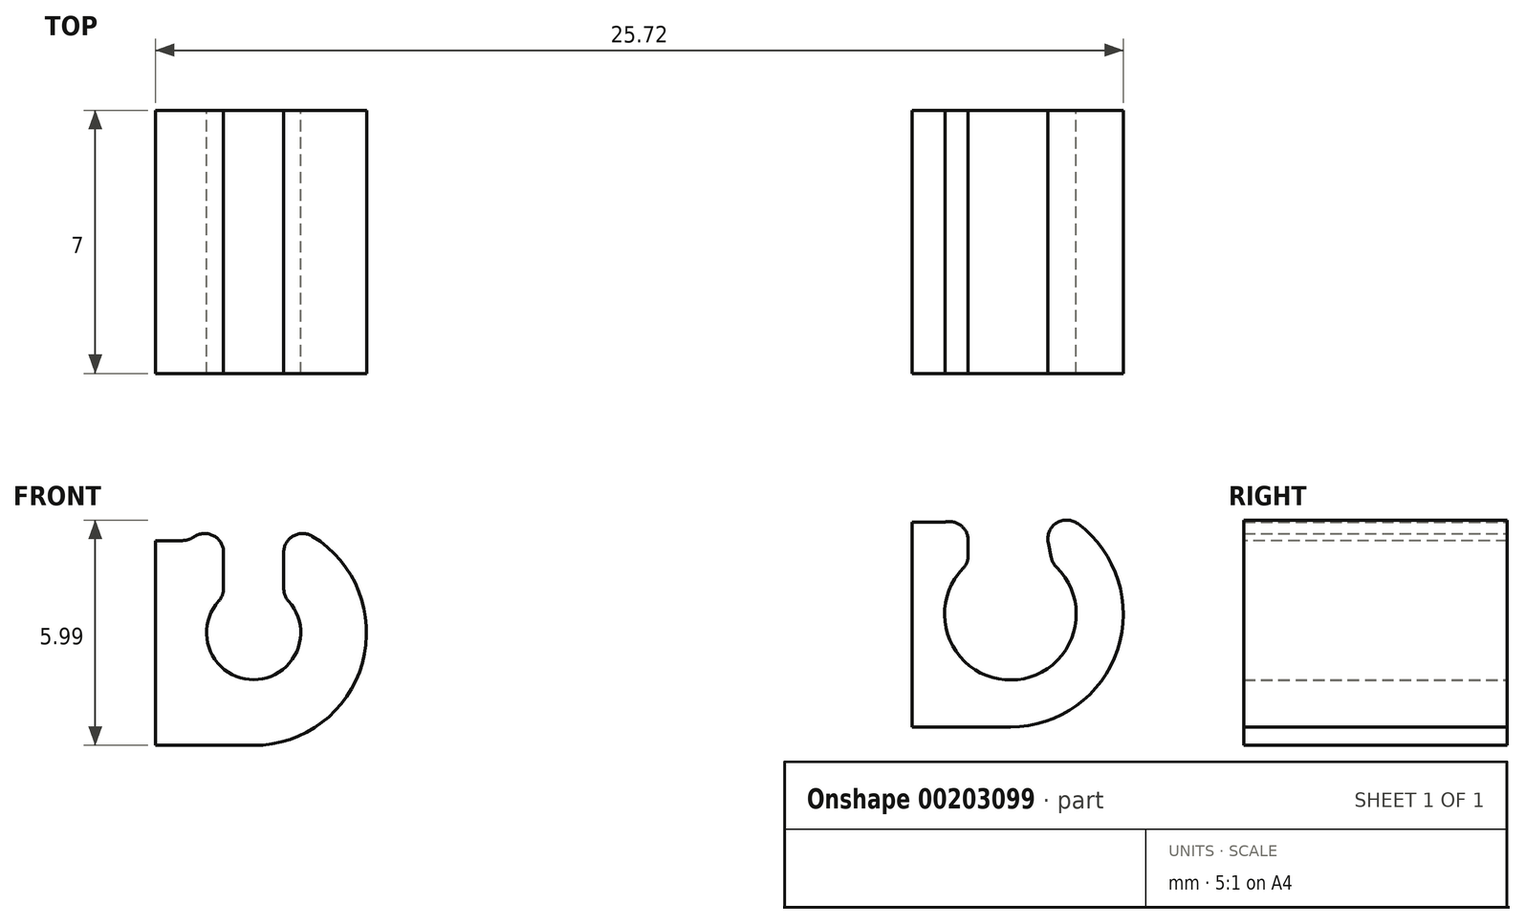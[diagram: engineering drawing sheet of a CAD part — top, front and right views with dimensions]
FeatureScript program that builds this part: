
annotation { "Feature Type Name" : "Feature", "Feature Type Description" : "" }
export const myFeature = defineFeature(function(context is Context, id is Id, definition is map)
    precondition{}
    {
        {
            var Q0;
            Q0=qCreatedBy(makeId("Front.planeOp"),FACE);
            var sketch = newSketch(context, id + "F0", { "sketchPlane" : qUnion([Q0])});
            skArc(sketch, "E0", {"start": v(-0.8, 2.9) * mm, "mid": v(-1.29, 2.71) * mm, "end": v(-1.73, 2.45) * mm});
            skArc(sketch, "E1", {"start": v(-0.8, 0.96) * mm, "mid": v(0, -1.25) * mm, "end": v(0.8, 0.96) * mm});
            skLineSegment(sketch, "E2", {"start": v(-0.8, 2.9) * mm, "end": v(-0.8, 0.96) * mm});
            skLineSegment(sketch, "E3.MirrorCS", {"start": v(0.8, 2.9) * mm, "end": v(0.8, 0.96) * mm});
            skLineSegment(sketch, "E4", {"start": v(-2.6, 1.48) * mm, "end": v(-2.6, -1.48) * mm});
            skArc(sketch, "E5.trimOffspring", {"start": v(0, -3) * mm, "mid": v(2.97, -0.4) * mm, "end": v(0.8, 2.9) * mm});
            skLineSegment(sketch, "E6", {"start": v(-2.6, 1.48) * mm, "end": v(-2.6, 2.45) * mm});
            skLineSegment(sketch, "E7", {"start": v(-2.6, -1.48) * mm, "end": v(-2.6, -3) * mm});
            skLineSegment(sketch, "E8", {"start": v(0, -3) * mm, "end": v(-2.6, -3) * mm});
            skLineSegment(sketch, "E9", {"start": v(-1.73, 2.45) * mm, "end": v(-2.6, 2.45) * mm});
            skArc(sketch, "E10", {"start": v(18.99, 3.27) * mm, "mid": v(18.67, 3.12) * mm, "end": v(18.37, 2.94) * mm});
            skArc(sketch, "E11", {"start": v(18.99, 1.83) * mm, "mid": v(20.1, -1.26) * mm, "end": v(21.23, 1.83) * mm});
            skLineSegment(sketch, "E12", {"start": v(18.99, 3.27) * mm, "end": v(18.99, 1.83) * mm});
            skLineSegment(sketch, "E13.MirrorCS", {"start": v(20.9, 3.38) * mm, "end": v(21.23, 1.83) * mm});
            skLineSegment(sketch, "E14", {"start": v(17.5, 1.97) * mm, "end": v(17.5, -1) * mm});
            skArc(sketch, "E15.trimOffspring", {"start": v(20.1, -2.51) * mm, "mid": v(23.08, 0.09) * mm, "end": v(20.9, 3.38) * mm});
            skLineSegment(sketch, "E16", {"start": v(17.5, 1.97) * mm, "end": v(17.5, 2.94) * mm});
            skLineSegment(sketch, "E17", {"start": v(17.5, -1) * mm, "end": v(17.5, -2.51) * mm});
            skLineSegment(sketch, "E18", {"start": v(20.1, -2.51) * mm, "end": v(17.5, -2.51) * mm});
            skLineSegment(sketch, "E19", {"start": v(18.37, 2.94) * mm, "end": v(17.5, 2.94) * mm});
            skSolve(sketch);
        }
        {
            var Q0;
            Q0 = qSketchRegion(id + "F0", true);
            extrude(context, id + "F1", {"entities" : qUnion([Q0]), "depth" : 7 * mm});
        }
        {
            var Q0;
            Q0=makeQuery(id+"F1.opExtrude","SWEPT_EDGE",EDGE,{"disambiguationData":[OSD([sQuery(id+"F0.wireOp",EDGE,"E0"),sQuery(id+"F0.wireOp",EDGE,"E2")])]});
            var Q1;
            Q1=makeQuery(id+"F1.opExtrude","SWEPT_EDGE",EDGE,{"disambiguationData":[OSD([sQuery(id+"F0.wireOp",EDGE,"E1"),sQuery(id+"F0.wireOp",EDGE,"E2")])]});
            var Q2;
            Q2=makeQuery(id+"F1.opExtrude","SWEPT_EDGE",EDGE,{"disambiguationData":[OSD([sQuery(id+"F0.wireOp",EDGE,"E1"),sQuery(id+"F0.wireOp",EDGE,"E3.MirrorCS")])]});
            var Q3;
            Q3=makeQuery(id+"F1.opExtrude","SWEPT_EDGE",EDGE,{"disambiguationData":[OSD([sQuery(id+"F0.wireOp",EDGE,"E0"),sQuery(id+"F0.wireOp",EDGE,"E3.MirrorCS")])]});
            fillet(context, id + "F2", {"entities" : qUnion([Q0, Q1, Q2, Q3]), "radius" : .5 * mm, "tangentPropagation" : true, "allowEdgeOverflow" : false});
        }
        {
            var Q0;
            Q0=makeQuery(id+"F1.opExtrude","SWEPT_EDGE",EDGE,{"disambiguationData":[OSD([sQuery(id+"F0.wireOp",EDGE,"E13.MirrorCS"),sQuery(id+"F0.wireOp",EDGE,"E15.trimOffspring")])]});
            var Q1;
            Q1=makeQuery(id+"F1.opExtrude","SWEPT_EDGE",EDGE,{"disambiguationData":[OSD([sQuery(id+"F0.wireOp",EDGE,"E11"),sQuery(id+"F0.wireOp",EDGE,"E13.MirrorCS")])]});
            var Q2;
            Q2=makeQuery(id+"F1.opExtrude","SWEPT_EDGE",EDGE,{"disambiguationData":[OSD([sQuery(id+"F0.wireOp",EDGE,"E10"),sQuery(id+"F0.wireOp",EDGE,"E12")])]});
            var Q3;
            Q3=makeQuery(id+"F1.opExtrude","SWEPT_EDGE",EDGE,{"disambiguationData":[OSD([sQuery(id+"F0.wireOp",EDGE,"E11"),sQuery(id+"F0.wireOp",EDGE,"E12")])]});
            fillet(context, id + "F3", {"entities" : qUnion([Q0, Q1, Q2, Q3]), "radius" : .5 * mm, "tangentPropagation" : true, "allowEdgeOverflow" : false});
        }
    });
